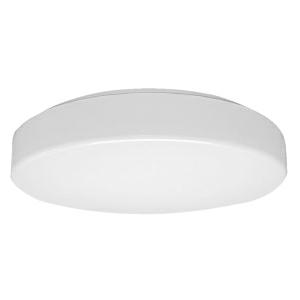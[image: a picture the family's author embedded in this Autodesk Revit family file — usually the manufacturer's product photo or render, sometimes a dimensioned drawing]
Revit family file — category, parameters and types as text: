
# Revit family: oblo_fit_-_oba_4000_840_00813353_08ec
name_source: partatom
category: Lighting Fixtures
units: mm (PartAtom-declared; Revit-internal decimal feet)

## family parameters
Cut with Voids When Loaded = No
Host = Face
Light Source = No
Part Type = Normal
Room Calculation Point = No
Round Connector Dimension = Use Diameter
Shared = No

## types (1)
- deko (1 x LED, 3350 lm, 4000K)
    Apparent Load = 44 VA
    Approval mark = CE
    CIE Flux Codes = 47 78 95 100 100
    Color Rendering = 80-89
    Color Temperature = 4000K
    Control Gear = Electronic ballast
    Default Elevation = 1800 mm
    Description = OBA 4000/840|Surface-mounted luminaire.|light source:   Cold white   |work equipment: Power supply unit|luminous flux: 4300 lm|light distribution: Direct|class of protection: I|technology: Switchable|mains lead: Direct power supply|glare control: without|
    Frequency = 50 Hz, 60 Hz
    Height = 95 mm
    Lamp = 1 x LED
    Lamp Light Flux = 3350 lm
    Lamp count = 1
    Length = 460 mm
    Luminous efficacy = 76 lm/W
    Manufacturer = Waldmann
    ModVariant = No
    Model = 00813353
    Mounting Place = Ceiling
    Mounting Type = Surface mounted
    Number of Poles = 1
    OnlyDefault = Yes
    Power Factor = 1
    Product Name = OBLO.fit - OBA 4000/840
    Product group = Ceiling mounted luminaire
    ProductGroupID = 3
    Protection Class = Protection class I
    Protection Degree = IP 40
    RLX_Detail_Level = 1
    RLX_Emergency_Light_Flux = 0 lm
    RLX_Emergency_Type = 0
    RLX_Emergency_Type_DB = No
    RlxData = <blob elided: 23493 chars, md5=f656a283>
    Socket = socket
    Standby Power = 0 W
    System Light Flux = 3350 lm
    System Power = 44 W
    Type Comments = mit Deko-Ring
    Type Image = oblo_led.jpg
    URL = http://relux.com
    VarID = deko
    Voltage = 230 V
    Voltage Range = 220-240 V
    Weight = 0.00 kg
    Width = 0 mm  [stored 0 ft]

note: [stored X ft] marks values corroborated as IEEE doubles in the binary element streams (Revit-internal decimal feet)

## geometry (parser evidence)
native form markers: Blend x4, Sweep x13
no freeform markers — native parametric forms only
